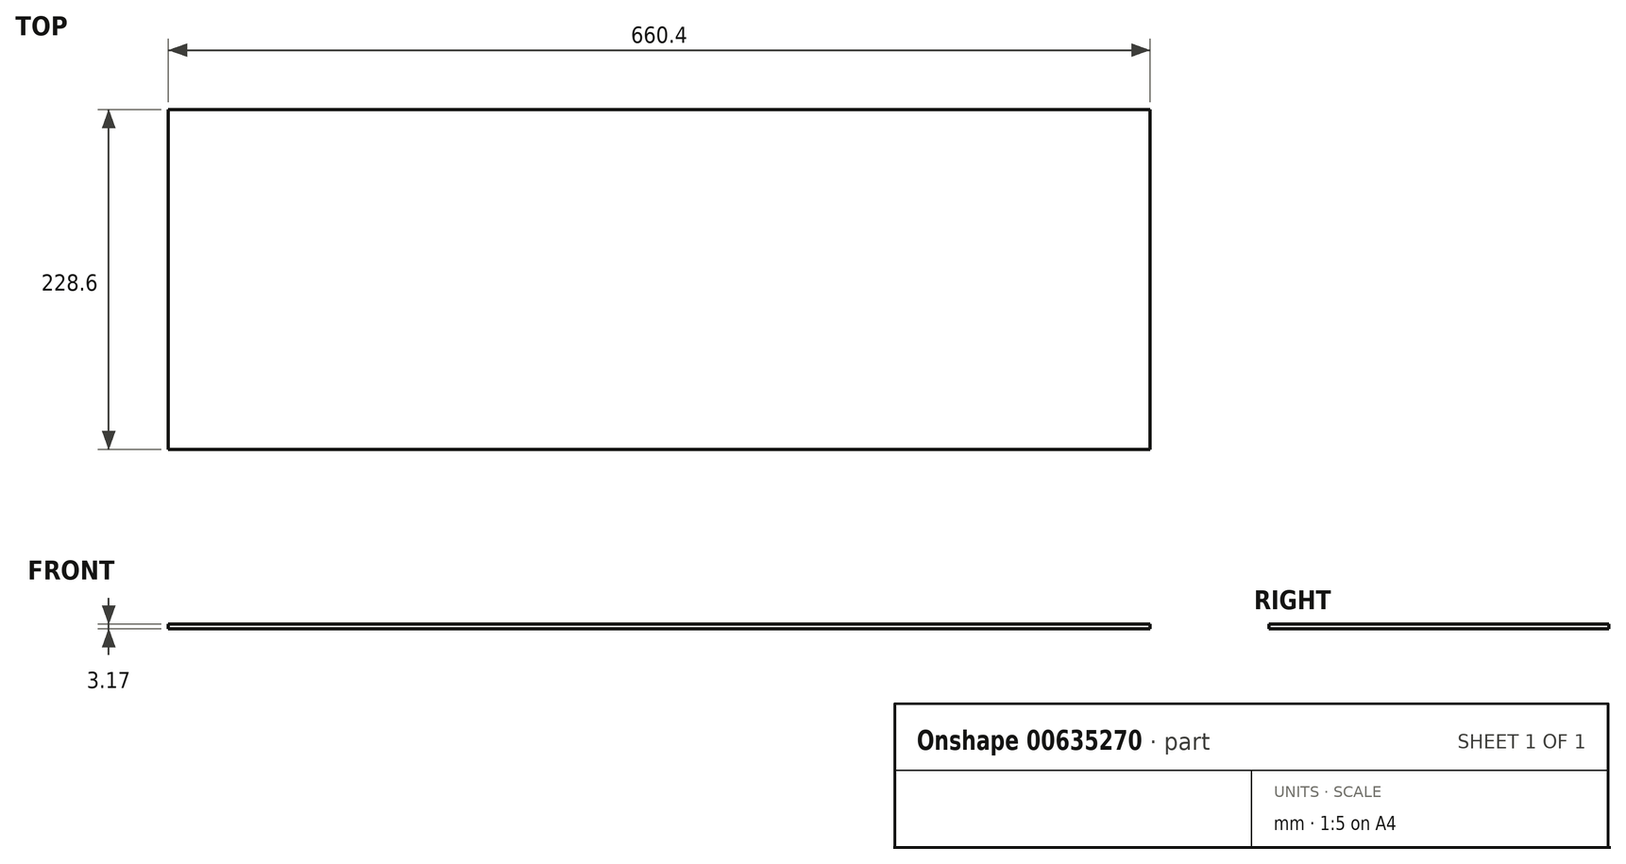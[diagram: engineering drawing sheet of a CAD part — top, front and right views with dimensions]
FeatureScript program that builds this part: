
annotation { "Feature Type Name" : "Feature", "Feature Type Description" : "" }
export const myFeature = defineFeature(function(context is Context, id is Id, definition is map)
    precondition{}
    {
        {
            var Q0;
            Q0=qCreatedBy(makeId("Top.planeOp"),FACE);
            var sketch = newSketch(context, id + "F0", { "sketchPlane" : qUnion([Q0])});
            skLineSegment(sketch, "E0.bottom", {"start": v(330.2, 114.3) * mm, "end": v(-330.2, 114.3) * mm});
            skLineSegment(sketch, "E0.top", {"start": v(330.2, -114.3) * mm, "end": v(-330.2, -114.3) * mm});
            skLineSegment(sketch, "E0.left", {"start": v(330.2, 114.3) * mm, "end": v(330.2, -114.3) * mm});
            skLineSegment(sketch, "E0.right", {"start": v(-330.2, 114.3) * mm, "end": v(-330.2, -114.3) * mm});
            skPoint(sketch, "E0.middle", {"position": v(0, 0) * mm});
            skSolve(sketch);
        }
        {
            var Q0;
            Q0=makeQuery(id+"F0.imprint","IMPRINT",FACE,{"disambiguationData":[TD([[makeQuery(id+"F0.imprint","IMPRINT",EDGE,{"derivedFrom":sQuery(id+"F0.wireOp",EDGE,"E0.bottom")}),1.0]])]});
            extrude(context, id + "F1", {"entities" : qUnion([Q0]), "depth" : 3.17 * mm, "offsetDistance" : 25.4 * mm});
        }
    });
